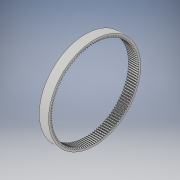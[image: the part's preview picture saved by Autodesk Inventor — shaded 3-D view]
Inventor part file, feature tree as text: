
AUTODESK INVENTOR PART (.ipt)
format: ipt  version: 2018 (Build 220112000, 112)  size: 1,717,248 bytes
history: native  units: mm
features: extrude x1, sketch x1
ambient origin geometry x8: Origin, YZ Plane, XZ Plane, XY Plane, X Axis, Y Axis, Z Axis, Center Point
bodies: Solid1 (feature_tree)
feature tree (2):
  extrude  "Extrusion1"  Depth=7.0mm
  sketch  "Sketch1"  dims[d0=70.0mm d1=67.26mm d2=65.0mm d3=0.2mm d4=0.13mm d5=0.66mm d6=7.34mm d7=1320.0mm d9=360.0deg d11=7.0mm d12=0.0mm]
